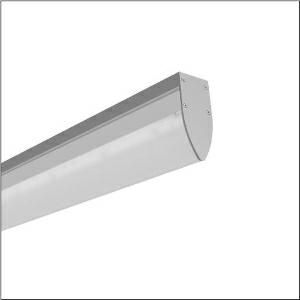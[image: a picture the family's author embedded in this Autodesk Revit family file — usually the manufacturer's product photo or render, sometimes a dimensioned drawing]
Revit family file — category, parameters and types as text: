
# Revit family: mira_21_td_51fr527p454a
name_source: partatom
category: Lighting Fixtures
units: mm (PartAtom-declared; Revit-internal decimal feet)

## family parameters
Cut with Voids When Loaded = No
Host = Face
Light Source = No
Part Type = Normal
Room Calculation Point = No
Round Connector Dimension = Use Diameter
Shared = No

## types (1)
- Mira 21 TD (1 x LED, 5040 lm, 34 W, 4000K)
    Apparent Load = 34 VA
    CIE Flux Codes = 40 68 87 81 100
    Color Rendering = 80
    Color Temperature = 4000K
    Default Elevation = 1800 mm
    Description = Mira 21 TD, clean room luminaire, primary light control with reflector, primary optical cover: cover, of PMMA, frosted, light emission: direct distribution, primary light characteristic: symmetric, installation type: surface-mounted, LED, rated luminous flux: 5.040lm, luminous efficacy: 148lm/W, light colour: 840, colour temperature: 4000K, control gear: ON/OFF, with terminal, 3-pole, max. 2.5mm², mains connection: 230V, AC, 50/60Hz, rated input power: 34W, luminaire housing, of sheet steel, coated, pure white (RAL 9010), length: 1.500mm, width: 55mm, height: 120mm, protection rating (complete): IP43, insulation class (complete): insulation class I (protective earthing), certification: CE, UKCA, permissible operating ambient temperature: -5..+40°C, standard: EN 50419, packaging unit: 1 piece
    Height = 120 mm
    Lamp = 1 x LED
    Lamp Light Flux = 5040 lm
    Lamp Power = 34 W
    Lamp count = 1
    Length = 1500 mm
    Luminous efficacy = 148 lm/W
    Manufacturer = Siteco
    ModVariant = No
    Model = 51FR527P454A
    Mounting Place = Ceiling
    Mounting Type = Surface mounted
    Number of Poles = 1
    OnlyDefault = Yes
    Power Factor = 1
    Product Name = Mira 21 TD
    Product group = clean room luminaire | ceiling mounted
    ProductGroupID = 306
    Protection Class = Protection class I
    Protection Degree = IP 43
    RLX_Detail_Level = 1
    RLX_Emergency_Light_Flux = 0 lm
    RLX_Emergency_Type = 0
    RLX_Emergency_Type_DB = No
    RlxData = <blob elided: 25201 chars, md5=a5ab23f1>
    Socket = socket
    Standby Power = 0 W
    System Light Flux = 5040 lm
    System Power = 34 W
    Type Comments = Product without accessories
    Type Image = l_1007115.jpg
    URL = http://relux.com
    VarID = ---
    Voltage = 0 V
    Weight = 0.00 kg
    Width = 55 mm

## geometry (parser evidence)
native form markers: Blend x4, Sweep x11
no freeform markers — native parametric forms only
